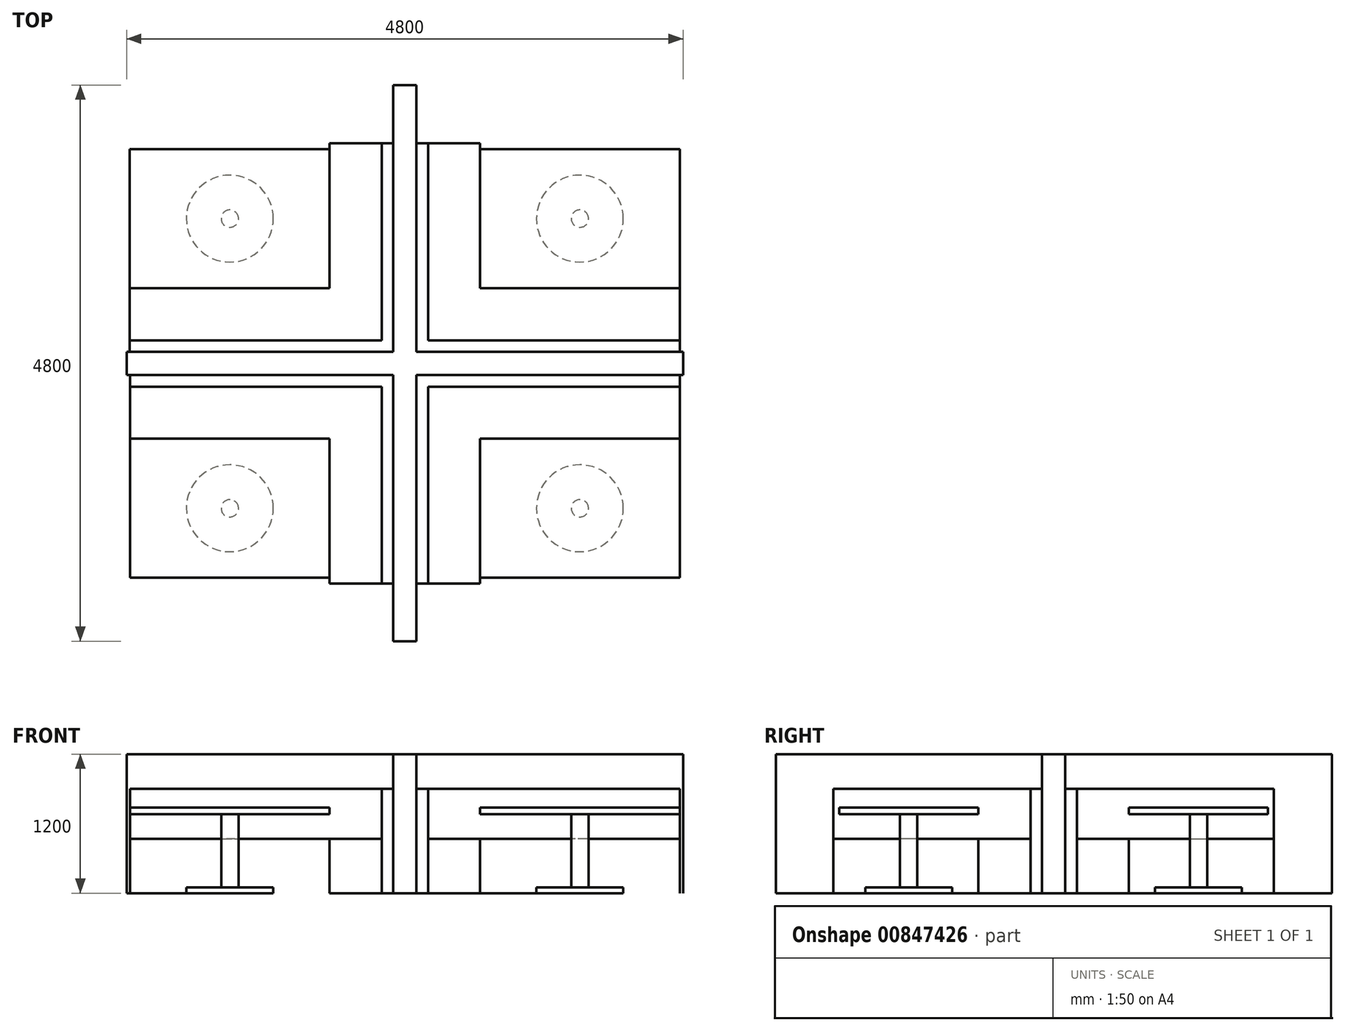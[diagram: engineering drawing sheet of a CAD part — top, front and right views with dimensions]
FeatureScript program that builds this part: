
annotation { "Feature Type Name" : "Feature", "Feature Type Description" : "" }
export const myFeature = defineFeature(function(context is Context, id is Id, definition is map)
    precondition{}
    {
        {
            var Q0;
            Q0=qCreatedBy(makeId("Top.planeOp"),FACE);
            var sketch = newSketch(context, id + "F0", { "sketchPlane" : qUnion([Q0])});
            skLineSegment(sketch, "E0", {"start": v(-100, -100) * mm, "end": v(-2298.01, -100) * mm, "construction": true});
            skLineSegment(sketch, "E1", {"start": v(-100, 1900) * mm, "end": v(-100, 100) * mm, "construction": true});
            skLineSegment(sketch, "E2", {"start": v(-200, 200) * mm, "end": v(-200, 1851.2) * mm, "construction": true});
            skLineSegment(sketch, "E3", {"start": v(-200, 1900) * mm, "end": v(-100, 1900) * mm, "construction": true});
            skLineSegment(sketch, "E4", {"start": v(-2373.01, 200) * mm, "end": v(-200, 200) * mm, "construction": true});
            skLineSegment(sketch, "E5", {"start": v(-100, 100) * mm, "end": v(-2373.01, 100) * mm, "construction": true});
            skLineSegment(sketch, "E6", {"start": v(-2373.01, 100) * mm, "end": v(-2373.01, 200) * mm, "construction": true});
            skLineSegment(sketch, "E7", {"start": v(-200, 1900) * mm, "end": v(-200, 200) * mm, "construction": true});
            skLineSegment(sketch, "E8", {"start": v(-650, 650) * mm, "end": v(-650, 1900) * mm, "construction": true});
            skLineSegment(sketch, "E9", {"start": v(-650, 1900) * mm, "end": v(-200, 1900) * mm, "construction": true});
            skLineSegment(sketch, "E10", {"start": v(-200, 200) * mm, "end": v(-2373.01, 200) * mm, "construction": true});
            skLineSegment(sketch, "E11", {"start": v(-2373.01, 200) * mm, "end": v(-2373.01, 650) * mm, "construction": true});
            skLineSegment(sketch, "E12", {"start": v(-2373.01, 650) * mm, "end": v(-650, 650) * mm, "construction": true});
            skLineSegment(sketch, "E13", {"start": v(100, 2207.12) * mm, "end": v(100, 100) * mm, "construction": true});
            skCircle(sketch, "E14", {"center": v(-407.83, 1500) * mm, "radius": 125 * mm, "construction": true});
            skCircle(sketch, "E15", {"center": v(-411.47, 900) * mm, "radius": 125 * mm, "construction": true});
            skCircle(sketch, "E16", {"center": v(-900, 411.47) * mm, "radius": 125 * mm, "construction": true});
            skCircle(sketch, "E17", {"center": v(-1500, 407.83) * mm, "radius": 125 * mm, "construction": true});
            skCircle(sketch, "E18", {"center": v(-2690.06, 950) * mm, "radius": 225 * mm, "construction": true});
            skCircle(sketch, "E19", {"center": v(-2690.06, 1550) * mm, "radius": 225 * mm, "construction": true});
            skCircle(sketch, "E20", {"center": v(-1550, 2201.47) * mm, "radius": 225 * mm, "construction": true});
            skCircle(sketch, "E21", {"center": v(-950, 2201.47) * mm, "radius": 225 * mm, "construction": true});
            skLineSegment(sketch, "E22", {"start": v(-2373.01, 1850) * mm, "end": v(-2373.01, 650) * mm, "construction": true});
            skLineSegment(sketch, "E23", {"start": v(-650, 650) * mm, "end": v(-650, 1850) * mm, "construction": true});
            skLineSegment(sketch, "E24", {"start": v(-650, 1850) * mm, "end": v(-2373.01, 1850) * mm, "construction": true});
            skCircle(sketch, "E25", {"center": v(-2100, 407.83) * mm, "radius": 125 * mm, "construction": true});
            skCircle(sketch, "E26", {"center": v(-2128.39, 2201.47) * mm, "radius": 225 * mm, "construction": true});
            skLineSegment(sketch, "E27", {"start": v(-100, -100) * mm, "end": v(-2400, -100) * mm, "construction": true});
            skLineSegment(sketch, "E28", {"start": v(-2400, -100) * mm, "end": v(-2400, 100) * mm, "construction": true});
            skLineSegment(sketch, "E29", {"start": v(-2400, 100) * mm, "end": v(-100, 100) * mm, "construction": true});
            skLineSegment(sketch, "E30", {"start": v(100, 100) * mm, "end": v(2400, 100) * mm, "construction": true});
            skLineSegment(sketch, "E31", {"start": v(2400, 100) * mm, "end": v(2400, -100) * mm, "construction": true});
            skLineSegment(sketch, "E32", {"start": v(2400, -100) * mm, "end": v(100, -100) * mm, "construction": true});
            skLineSegment(sketch, "E33", {"start": v(100, -100) * mm, "end": v(100, -2396.97) * mm, "construction": true});
            skLineSegment(sketch, "E34", {"start": v(100, -2396.97) * mm, "end": v(-100, -2396.97) * mm, "construction": true});
            skLineSegment(sketch, "E35", {"start": v(-100, -2396.97) * mm, "end": v(-100, -100) * mm, "construction": true});
            skLineSegment(sketch, "E36", {"start": v(-100, 100) * mm, "end": v(-100, 2403.03) * mm, "construction": true});
            skLineSegment(sketch, "E37", {"start": v(-100, 2403.03) * mm, "end": v(100, 2403.03) * mm, "construction": true});
            skLineSegment(sketch, "E38", {"start": v(100, 2403.03) * mm, "end": v(100, 100) * mm, "construction": true});
            skLineSegment(sketch, "E39", {"start": v(200, 200) * mm, "end": v(200, 1851.2) * mm, "construction": true});
            skLineSegment(sketch, "E40", {"start": v(200, 1900) * mm, "end": v(100, 1900) * mm, "construction": true});
            skLineSegment(sketch, "E41", {"start": v(2373.01, 200) * mm, "end": v(200, 200) * mm, "construction": true});
            skLineSegment(sketch, "E42", {"start": v(2373.01, 100) * mm, "end": v(2373.01, 200) * mm, "construction": true});
            skLineSegment(sketch, "E43", {"start": v(200, 1900) * mm, "end": v(200, 200) * mm, "construction": true});
            skLineSegment(sketch, "E44", {"start": v(650, 650) * mm, "end": v(650, 1900) * mm, "construction": true});
            skLineSegment(sketch, "E45", {"start": v(650, 1900) * mm, "end": v(200, 1900) * mm, "construction": true});
            skLineSegment(sketch, "E46", {"start": v(200, 200) * mm, "end": v(2373.01, 200) * mm, "construction": true});
            skLineSegment(sketch, "E47", {"start": v(2373.01, 200) * mm, "end": v(2373.01, 650) * mm, "construction": true});
            skLineSegment(sketch, "E48", {"start": v(2373.01, 650) * mm, "end": v(650, 650) * mm, "construction": true});
            skCircle(sketch, "E49", {"center": v(407.83, 1500) * mm, "radius": 125 * mm, "construction": true});
            skCircle(sketch, "E50", {"center": v(411.47, 900) * mm, "radius": 125 * mm, "construction": true});
            skCircle(sketch, "E51", {"center": v(900, 411.47) * mm, "radius": 125 * mm, "construction": true});
            skCircle(sketch, "E52", {"center": v(1500, 407.83) * mm, "radius": 125 * mm, "construction": true});
            skCircle(sketch, "E53", {"center": v(2690.06, 950) * mm, "radius": 225 * mm, "construction": true});
            skCircle(sketch, "E54", {"center": v(2690.06, 1550) * mm, "radius": 225 * mm, "construction": true});
            skCircle(sketch, "E55", {"center": v(1550, 2201.47) * mm, "radius": 225 * mm, "construction": true});
            skCircle(sketch, "E56", {"center": v(950, 2201.47) * mm, "radius": 225 * mm, "construction": true});
            skLineSegment(sketch, "E57", {"start": v(2373.01, 1850) * mm, "end": v(2373.01, 650) * mm, "construction": true});
            skLineSegment(sketch, "E58", {"start": v(650, 650) * mm, "end": v(650, 1850) * mm, "construction": true});
            skLineSegment(sketch, "E59", {"start": v(650, 1850) * mm, "end": v(2373.01, 1850) * mm, "construction": true});
            skCircle(sketch, "E60", {"center": v(2100, 407.83) * mm, "radius": 125 * mm, "construction": true});
            skCircle(sketch, "E61", {"center": v(2128.39, 2201.47) * mm, "radius": 225 * mm, "construction": true});
            skLineSegment(sketch, "E62", {"start": v(-200, -200) * mm, "end": v(-200, -1851.2) * mm, "construction": true});
            skLineSegment(sketch, "E63", {"start": v(-2370.01, -200) * mm, "end": v(-200, -200) * mm, "construction": true});
            skLineSegment(sketch, "E64", {"start": v(-200, -1901.2) * mm, "end": v(-200, -200) * mm, "construction": true});
            skLineSegment(sketch, "E65", {"start": v(-650, -650) * mm, "end": v(-650, -1901.2) * mm, "construction": true});
            skLineSegment(sketch, "E66", {"start": v(-650, -1901.2) * mm, "end": v(-200, -1901.2) * mm, "construction": true});
            skLineSegment(sketch, "E67", {"start": v(-200, -200) * mm, "end": v(-2370.01, -200) * mm, "construction": true});
            skLineSegment(sketch, "E68", {"start": v(-2370.01, -200) * mm, "end": v(-2370.01, -650) * mm, "construction": true});
            skLineSegment(sketch, "E69", {"start": v(-2370.01, -650) * mm, "end": v(-650, -650) * mm, "construction": true});
            skCircle(sketch, "E70", {"center": v(-407.83, -1500) * mm, "radius": 125 * mm, "construction": true});
            skCircle(sketch, "E71", {"center": v(-411.47, -900) * mm, "radius": 125 * mm, "construction": true});
            skCircle(sketch, "E72", {"center": v(-900, -411.47) * mm, "radius": 125 * mm, "construction": true});
            skCircle(sketch, "E73", {"center": v(-1500, -407.83) * mm, "radius": 125 * mm, "construction": true});
            skCircle(sketch, "E74", {"center": v(-2690.06, -950) * mm, "radius": 225 * mm, "construction": true});
            skCircle(sketch, "E75", {"center": v(-2690.06, -1550) * mm, "radius": 225 * mm, "construction": true});
            skCircle(sketch, "E76", {"center": v(-1550, -2201.47) * mm, "radius": 225 * mm, "construction": true});
            skCircle(sketch, "E77", {"center": v(-950, -2201.47) * mm, "radius": 225 * mm, "construction": true});
            skLineSegment(sketch, "E78", {"start": v(-2370.01, -1850) * mm, "end": v(-2370.01, -650) * mm, "construction": true});
            skLineSegment(sketch, "E79", {"start": v(-650, -650) * mm, "end": v(-650, -1850) * mm, "construction": true});
            skLineSegment(sketch, "E80", {"start": v(-650, -1850) * mm, "end": v(-2370.01, -1850) * mm, "construction": true});
            skCircle(sketch, "E81", {"center": v(-2100, -407.83) * mm, "radius": 125 * mm, "construction": true});
            skCircle(sketch, "E82", {"center": v(-2128.39, -2201.47) * mm, "radius": 225 * mm, "construction": true});
            skLineSegment(sketch, "E83", {"start": v(-2370.01, -100) * mm, "end": v(-2370.01, -200) * mm, "construction": true});
            skLineSegment(sketch, "E84", {"start": v(-200, -1901.2) * mm, "end": v(-100, -1901.2) * mm, "construction": true});
            skLineSegment(sketch, "E85", {"start": v(200, -200) * mm, "end": v(200, -1851.2) * mm, "construction": true});
            skLineSegment(sketch, "E86", {"start": v(2373.01, -200) * mm, "end": v(200, -200) * mm, "construction": true});
            skLineSegment(sketch, "E87", {"start": v(200, -1901.2) * mm, "end": v(200, -200) * mm, "construction": true});
            skLineSegment(sketch, "E88", {"start": v(650, -650) * mm, "end": v(650, -1901.2) * mm, "construction": true});
            skLineSegment(sketch, "E89", {"start": v(650, -1901.2) * mm, "end": v(200, -1901.2) * mm, "construction": true});
            skLineSegment(sketch, "E90", {"start": v(200, -200) * mm, "end": v(2373.01, -200) * mm, "construction": true});
            skLineSegment(sketch, "E91", {"start": v(2373.01, -200) * mm, "end": v(2373.01, -650) * mm, "construction": true});
            skLineSegment(sketch, "E92", {"start": v(2373.01, -650) * mm, "end": v(650, -650) * mm, "construction": true});
            skCircle(sketch, "E93", {"center": v(407.83, -1500) * mm, "radius": 125 * mm, "construction": true});
            skCircle(sketch, "E94", {"center": v(411.47, -900) * mm, "radius": 125 * mm, "construction": true});
            skCircle(sketch, "E95", {"center": v(900, -411.47) * mm, "radius": 125 * mm, "construction": true});
            skCircle(sketch, "E96", {"center": v(1500, -407.83) * mm, "radius": 125 * mm, "construction": true});
            skCircle(sketch, "E97", {"center": v(2690.06, -950) * mm, "radius": 225 * mm, "construction": true});
            skCircle(sketch, "E98", {"center": v(2690.06, -1550) * mm, "radius": 225 * mm, "construction": true});
            skCircle(sketch, "E99", {"center": v(1550, -2201.47) * mm, "radius": 225 * mm, "construction": true});
            skCircle(sketch, "E100", {"center": v(950, -2201.47) * mm, "radius": 225 * mm, "construction": true});
            skLineSegment(sketch, "E101", {"start": v(2373.01, -1850) * mm, "end": v(2373.01, -650) * mm, "construction": true});
            skLineSegment(sketch, "E102", {"start": v(650, -650) * mm, "end": v(650, -1850) * mm, "construction": true});
            skLineSegment(sketch, "E103", {"start": v(650, -1850) * mm, "end": v(2373.01, -1850) * mm, "construction": true});
            skCircle(sketch, "E104", {"center": v(2100, -407.83) * mm, "radius": 125 * mm, "construction": true});
            skCircle(sketch, "E105", {"center": v(2128.39, -2201.47) * mm, "radius": 225 * mm, "construction": true});
            skLineSegment(sketch, "E106", {"start": v(2373.01, -100) * mm, "end": v(2373.01, -200) * mm, "construction": true});
            skLineSegment(sketch, "E107", {"start": v(200, -1901.2) * mm, "end": v(100, -1901.2) * mm, "construction": true});
            skSolve(sketch);
        }
        {
            var Q0;
            Q0=qCreatedBy(makeId("Top.planeOp"),FACE);
            cPlane(context, id + "F1", {"entities" : qUnion([Q0]), "cplaneType" : CPlaneType.OFFSET, "offset" : 0 * mm, "width" : 150 * mm, "height" : 150 * mm});
        }
        {
            var Q0;
            Q0=qCreatedBy(id+"F1.planeOp",FACE);
            cPlane(context, id + "F2", {"entities" : qUnion([Q0]), "cplaneType" : CPlaneType.OFFSET, "offset" : 470 * mm, "width" : 150 * mm, "height" : 150 * mm});
        }
        {
            var Q0;
            Q0=qCreatedBy(id+"F1.planeOp",FACE);
            cPlane(context, id + "F3", {"entities" : qUnion([Q0]), "cplaneType" : CPlaneType.OFFSET, "offset" : 900 * mm, "width" : 150 * mm, "height" : 150 * mm});
        }
        {
            var Q0;
            Q0=qCreatedBy(id+"F1.planeOp",FACE);
            cPlane(context, id + "F4", {"entities" : qUnion([Q0]), "cplaneType" : CPlaneType.OFFSET, "offset" : 1200 * mm, "width" : 150 * mm, "height" : 150 * mm});
        }
        {
            var Q0;
            Q0=qCreatedBy(id+"F2.planeOp",FACE);
            var sketch = newSketch(context, id + "F5", { "sketchPlane" : qUnion([Q0])});
            skLineSegment(sketch, "E108.0", {"start": v(-2373.01, 650) * mm, "end": v(-650, 650) * mm});
            skLineSegment(sketch, "E109.0", {"start": v(-2373.01, 200) * mm, "end": v(-2373.01, 650) * mm});
            skLineSegment(sketch, "E110.0", {"start": v(-200, 200) * mm, "end": v(-2373.01, 200) * mm});
            skLineSegment(sketch, "E111.0", {"start": v(-200, 1900) * mm, "end": v(-200, 200) * mm});
            skLineSegment(sketch, "E112.0", {"start": v(-650, 1900) * mm, "end": v(-200, 1900) * mm});
            skLineSegment(sketch, "E113.0", {"start": v(-650, 650) * mm, "end": v(-650, 1900) * mm});
            skLineSegment(sketch, "E114.0", {"start": v(650, 1900) * mm, "end": v(200, 1900) * mm});
            skLineSegment(sketch, "E115.0", {"start": v(200, 200) * mm, "end": v(200, 1900) * mm});
            skLineSegment(sketch, "E116.0", {"start": v(200, 200) * mm, "end": v(2373.01, 200) * mm});
            skLineSegment(sketch, "E117.0", {"start": v(2373.01, 650) * mm, "end": v(650, 650) * mm});
            skLineSegment(sketch, "E118.0", {"start": v(650, 650) * mm, "end": v(650, 1900) * mm});
            skLineSegment(sketch, "E119.0", {"start": v(-200, -200) * mm, "end": v(-2370.01, -200) * mm});
            skLineSegment(sketch, "E120.0", {"start": v(-2370.01, -200) * mm, "end": v(-2370.01, -650) * mm});
            skLineSegment(sketch, "E121.0", {"start": v(-2370.01, -650) * mm, "end": v(-650, -650) * mm});
            skLineSegment(sketch, "E122.0", {"start": v(-650, -650) * mm, "end": v(-650, -1901.2) * mm});
            skLineSegment(sketch, "E123.0", {"start": v(-650, -1901.2) * mm, "end": v(-200, -1901.2) * mm});
            skLineSegment(sketch, "E124.0", {"start": v(-200, -1901.2) * mm, "end": v(-200, -200) * mm});
            skLineSegment(sketch, "E125.0", {"start": v(650, -1901.2) * mm, "end": v(200, -1901.2) * mm});
            skLineSegment(sketch, "E126.0", {"start": v(200, -200) * mm, "end": v(200, -1901.2) * mm});
            skLineSegment(sketch, "E127.0", {"start": v(650, -650) * mm, "end": v(650, -1901.2) * mm});
            skLineSegment(sketch, "E128.0", {"start": v(2373.01, -650) * mm, "end": v(650, -650) * mm});
            skLineSegment(sketch, "E129.0", {"start": v(200, -200) * mm, "end": v(2373.01, -200) * mm});
            skLineSegment(sketch, "E130.0", {"start": v(2373.01, -200) * mm, "end": v(2373.01, -650) * mm});
            skLineSegment(sketch, "E131.0", {"start": v(2373.01, 200) * mm, "end": v(2373.01, 650) * mm});
            skSolve(sketch);
        }
        {
            var Q0;
            Q0 = qSketchRegion(id + "F5", true);
            extrude(context, id + "F6", {"entities" : qUnion([Q0]), "depth" : -470 * mm, "offsetDistance" : 25 * mm});
        }
        {
            var Q0;
            Q0=qCreatedBy(id+"F4.planeOp",FACE);
            var sketch = newSketch(context, id + "F7", { "sketchPlane" : qUnion([Q0])});
            skLineSegment(sketch, "E132.0", {"start": v(-100, 2403.03) * mm, "end": v(100, 2403.03) * mm});
            skLineSegment(sketch, "E133.0", {"start": v(-100, 100) * mm, "end": v(-100, 2403.03) * mm});
            skLineSegment(sketch, "E134.0", {"start": v(100, 2403.03) * mm, "end": v(100, 100) * mm});
            skLineSegment(sketch, "E135.0", {"start": v(-100, 100) * mm, "end": v(-2400, 100) * mm});
            skLineSegment(sketch, "E136.0", {"start": v(100, 100) * mm, "end": v(2400, 100) * mm});
            skLineSegment(sketch, "E137.0", {"start": v(2400, -100) * mm, "end": v(100, -100) * mm});
            skLineSegment(sketch, "E138.0", {"start": v(-100, -100) * mm, "end": v(-2400, -100) * mm});
            skLineSegment(sketch, "E139.0", {"start": v(-100, -2396.97) * mm, "end": v(-100, -100) * mm});
            skLineSegment(sketch, "E140.0", {"start": v(100, -100) * mm, "end": v(100, -2396.97) * mm});
            skLineSegment(sketch, "E141.0", {"start": v(-2400, -100) * mm, "end": v(-2400, 100) * mm});
            skLineSegment(sketch, "E142.0", {"start": v(2400, 100) * mm, "end": v(2400, -100) * mm});
            skLineSegment(sketch, "E143.0", {"start": v(100, -2396.97) * mm, "end": v(-100, -2396.97) * mm});
            skSolve(sketch);
        }
        {
            var Q0;
            Q0 = qSketchRegion(id + "F7", true);
            extrude(context, id + "F8", {"entities" : qUnion([Q0]), "depth" : -1200 * mm, "offsetDistance" : 25 * mm});
        }
        {
            var Q0;
            Q0=qCreatedBy(id+"F3.planeOp",FACE);
            var sketch = newSketch(context, id + "F9", { "sketchPlane" : qUnion([Q0])});
            skLineSegment(sketch, "E144.0", {"start": v(-2370.01, -100) * mm, "end": v(-2370.01, -200) * mm});
            skLineSegment(sketch, "E145.0", {"start": v(-200, -200) * mm, "end": v(-2370.01, -200) * mm});
            skLineSegment(sketch, "E146.0", {"start": v(-200, -1901.2) * mm, "end": v(-200, -200) * mm});
            skLineSegment(sketch, "E147.0", {"start": v(-200, -1901.2) * mm, "end": v(-100, -1901.2) * mm});
            skLineSegment(sketch, "E148.0", {"start": v(200, -1901.2) * mm, "end": v(100, -1901.2) * mm});
            skLineSegment(sketch, "E149.0", {"start": v(-200, 1900) * mm, "end": v(-100, 1900) * mm});
            skLineSegment(sketch, "E150.0", {"start": v(200, 1900) * mm, "end": v(100, 1900) * mm});
            skLineSegment(sketch, "E151.0", {"start": v(2373.01, 100) * mm, "end": v(2373.01, 200) * mm});
            skLineSegment(sketch, "E152.0", {"start": v(2373.01, -100) * mm, "end": v(2373.01, -200) * mm});
            skLineSegment(sketch, "E153.0", {"start": v(200, -1901.2) * mm, "end": v(200, -200) * mm});
            skLineSegment(sketch, "E154.0", {"start": v(-200, 1900) * mm, "end": v(-200, 200) * mm});
            skLineSegment(sketch, "E155.0", {"start": v(200, 1900) * mm, "end": v(200, 200) * mm});
            skLineSegment(sketch, "E156.0", {"start": v(-2373.01, 100) * mm, "end": v(-2373.01, 200) * mm});
            skLineSegment(sketch, "E157.0", {"start": v(-100, 100) * mm, "end": v(-2373.01, 100) * mm});
            skLineSegment(sketch, "E158.0", {"start": v(-100, 1900) * mm, "end": v(-100, 100) * mm});
            skLineSegment(sketch, "E159.0", {"start": v(-100, -100) * mm, "end": v(-2370.01, -100) * mm});
            skLineSegment(sketch, "E160.0", {"start": v(-100, -1901.2) * mm, "end": v(-100, -100) * mm});
            skLineSegment(sketch, "E161.0", {"start": v(100, -100) * mm, "end": v(100, -1901.2) * mm});
            skLineSegment(sketch, "E162.0", {"start": v(2373.01, -100) * mm, "end": v(100, -100) * mm});
            skLineSegment(sketch, "E163.0", {"start": v(100, 1900) * mm, "end": v(100, 100) * mm});
            skLineSegment(sketch, "E164.0", {"start": v(-200, 200) * mm, "end": v(-2373.01, 200) * mm});
            skLineSegment(sketch, "E165.0", {"start": v(100, 100) * mm, "end": v(2373.01, 100) * mm});
            skLineSegment(sketch, "E166.0", {"start": v(200, 200) * mm, "end": v(2373.01, 200) * mm});
            skLineSegment(sketch, "E167.0", {"start": v(200, -200) * mm, "end": v(2373.01, -200) * mm});
            skSolve(sketch);
        }
        {
            var Q0;
            Q0 = qSketchRegion(id + "F9", true);
            extrude(context, id + "F10", {"entities" : qUnion([Q0]), "depth" : -900 * mm, "offsetDistance" : 25 * mm});
        }
        {
            var Q0;
            Q0=qCreatedBy(makeId("Top.planeOp"),FACE);
            cPlane(context, id + "F11", {"entities" : qUnion([Q0]), "cplaneType" : CPlaneType.OFFSET, "offset" : 740 * mm, "width" : 150 * mm, "height" : 150 * mm});
        }
        {
            var Q0;
            Q0=qCreatedBy(id+"F11.planeOp",FACE);
            var sketch = newSketch(context, id + "F12", { "sketchPlane" : qUnion([Q0])});
            skLineSegment(sketch, "E168.0", {"start": v(-2373.01, 1850) * mm, "end": v(-2373.01, 650) * mm});
            skLineSegment(sketch, "E169.0", {"start": v(-2373.01, 650) * mm, "end": v(-650, 650) * mm});
            skLineSegment(sketch, "E170.0", {"start": v(-650, 1850) * mm, "end": v(-2373.01, 1850) * mm});
            skLineSegment(sketch, "E171.0", {"start": v(-650, 650) * mm, "end": v(-650, 1850) * mm});
            skLineSegment(sketch, "E172.0", {"start": v(-2370.01, -650) * mm, "end": v(-650, -650) * mm});
            skLineSegment(sketch, "E173.0", {"start": v(-2370.01, -1850) * mm, "end": v(-2370.01, -650) * mm});
            skLineSegment(sketch, "E174.0", {"start": v(-650, -1850) * mm, "end": v(-2370.01, -1850) * mm});
            skLineSegment(sketch, "E175.0", {"start": v(-650, -650) * mm, "end": v(-650, -1850) * mm});
            skLineSegment(sketch, "E176.0", {"start": v(650, -650) * mm, "end": v(650, -1850) * mm});
            skLineSegment(sketch, "E177.0", {"start": v(2373.01, -650) * mm, "end": v(650, -650) * mm});
            skLineSegment(sketch, "E178.0", {"start": v(2373.01, -1850) * mm, "end": v(2373.01, -650) * mm});
            skLineSegment(sketch, "E179.0", {"start": v(650, -1850) * mm, "end": v(2373.01, -1850) * mm});
            skLineSegment(sketch, "E180.0", {"start": v(2373.01, 1850) * mm, "end": v(2373.01, 650) * mm});
            skLineSegment(sketch, "E181.0", {"start": v(650, 1850) * mm, "end": v(2373.01, 1850) * mm});
            skLineSegment(sketch, "E182.0", {"start": v(650, 650) * mm, "end": v(650, 1850) * mm});
            skLineSegment(sketch, "E183.0", {"start": v(2373.01, 650) * mm, "end": v(650, 650) * mm});
            skSolve(sketch);
        }
        {
            var Q0;
            Q0 = qSketchRegion(id + "F12", true);
            extrude(context, id + "F13", {"entities" : qUnion([Q0]), "depth" : -60 * mm, "offsetDistance" : 25 * mm});
        }
        {
            var Q0;
            Q0=qCreatedBy(makeId("Top.planeOp"),FACE);
            var sketch = newSketch(context, id + "F14", { "sketchPlane" : qUnion([Q0])});
            skCircle(sketch, "E184", {"center": v(-1510, 1250) * mm, "radius": 375 * mm});
            skLineSegment(sketch, "E185", {"start": v(0, 0) * mm, "end": v(0, 1017.9) * mm, "construction": true});
            skLineSegment(sketch, "E186", {"start": v(0, 0) * mm, "end": v(-742.22, 0) * mm, "construction": true});
            skCircle(sketch, "E187.MirrorC", {"center": v(-1510, -1250) * mm, "radius": 375 * mm});
            skCircle(sketch, "E188.MirrorC", {"center": v(1510, 1250) * mm, "radius": 375 * mm});
            skCircle(sketch, "E189.MirrorC", {"center": v(1510, -1250) * mm, "radius": 375 * mm});
            skSolve(sketch);
        }
        {
            var Q0;
            Q0 = qSketchRegion(id + "F14", true);
            extrude(context, id + "F15", {"entities" : qUnion([Q0]), "depth" : 50 * mm, "offsetDistance" : 25 * mm});
        }
        {
            var Q0;
            Q0=makeQuery(id+"F15.opExtrude","CAP_FACE",FACE,{"disambiguationData":[OSD([sQuery(id+"F14.wireOp",EDGE,"E184")])],"isStart":false});
            var sketch = newSketch(context, id + "F16", { "sketchPlane" : qUnion([Q0])});
            skCircle(sketch, "E190.0", {"center": v(-1510, 1250) * mm, "radius": 75 * mm});
            skCircle(sketch, "E191.0", {"center": v(1510, 1250) * mm, "radius": 75 * mm});
            skCircle(sketch, "E192.0", {"center": v(-1510, -1250) * mm, "radius": 75 * mm});
            skCircle(sketch, "E193.0", {"center": v(1510, -1250) * mm, "radius": 75 * mm});
            skSolve(sketch);
        }
        {
            var Q0;
            Q0 = qSketchRegion(id + "F16", true);
            extrude(context, id + "F17", {"entities" : qUnion([Q0]), "endBound" : BoundingType.UP_TO_NEXT, "depth" : 25 * mm, "offsetDistance" : 25 * mm});
        }
    });
